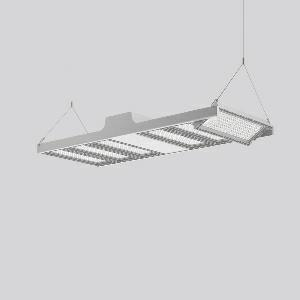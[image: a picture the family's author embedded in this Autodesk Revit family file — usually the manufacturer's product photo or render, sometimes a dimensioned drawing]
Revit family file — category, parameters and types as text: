
# Revit family: light_case_921691_004_1_76_25c0
name_source: partatom
category: Lighting Fixtures
units: mm (PartAtom-declared; Revit-internal decimal feet)

## family parameters
Cut with Voids When Loaded = No
Host = Face
Light Source = No
Part Type = Normal
Room Calculation Point = No
Round Connector Dimension = Use Diameter
Shared = No

## types (1)
- LIGHT CASE (1 x LED Modul 865, 8700 lm, 6500)
    Apparent Load = 335 VA
    CIE Flux Codes = 80 98 100 100 100
    Color Rendering = 80
    Color Temperature = 6500
    Default Elevation = 1800 mm
    Description = Series: LIGHT CASE
Flat highbay luminaire for chain or cable suspension with 6 LED modules that can be swivelled. Housing: die cast aluminium and sheet steel, powder-coated. Optimised thermal management thanks to special luminaire design. Self-cleaning heat sink for constant heat dissipation. Cover: plastic (polycarbonate, shockproof), with integrated four-row lens system. LED modules can be swivelled ± 30° for optimum illumination. CLO control for constant light output over the entire service life. Suitable for chain or steel cable suspension (to be provided on site). With 5-pin connection terminal (1.5 m). With integrated movement sensor and light sensor for daylight detection on request. Ball impact proof in accordance with DIN 18032-03 (except steel cable suspension). Luminaire with limited surface temperature in accordance with EN 60598-2-24 for use in environments in which a deposit of conductive dust on the luminaire can be expected. 
Colour: silver, matt (approx. RAL 9006)
Length: 956 mm
Width: 397 mm
Height: 110 mm
Lamp: LED
Socket: without socket
Colour temperature: 6500K
Colour rendering index (CRI): 80
System power: 335 W
Rated luminous flux: 52200 lm
Luminous efficiency: 156 lm/W
Control gear: Converter, dimmable, DALI
Protection class: I
Type of protection: IP 65
    Height = 110 mm
    Lamp = 1 x LED Modul 865
    Lamp Light Flux = 8700 lm
    Lamp count = 1
    Length = 956 mm
    Lifetime = 50000 h
    Luminous efficacy = 156 lm/W
    Manufacturer = RZB
    ModVariant = No
    Model = 921691.004.1.76
    Mounting Place = Ceiling
    Mounting Type = Pendant
    Number of Poles = 1
    OnlyDefault = Yes
    Power Factor = 1
    Product Name = LIGHT CASE
    Product group = Pendant commercial luminaires
    ProductGroupID = 903
    Protection Class = Protection class I
    Protection Degree = IP 65
    RLX_Detail_Level = 1
    RLX_Emergency_Light_Flux = 0 lm
    RLX_Emergency_Type = 0
    RLX_Emergency_Type_DB = No
    RlxData = <blob elided: 31529 chars, md5=b1f299bc>
    Socket = socket
    Standby Power = 0 W
    System Light Flux = 52200 lm
    System Power = 335 W
    Type Comments = Product without accessories
    Type Image = 921526.004.76.jpg
    URL = http://relux.com
    VarID = ---
    Voltage = 230 V
    Voltage Range = 220-240 V
    Weight = 0.00 kg
    Width = 397 mm

## geometry (parser evidence)
native form markers: Blend x4, Sweep x22
no freeform markers — native parametric forms only
